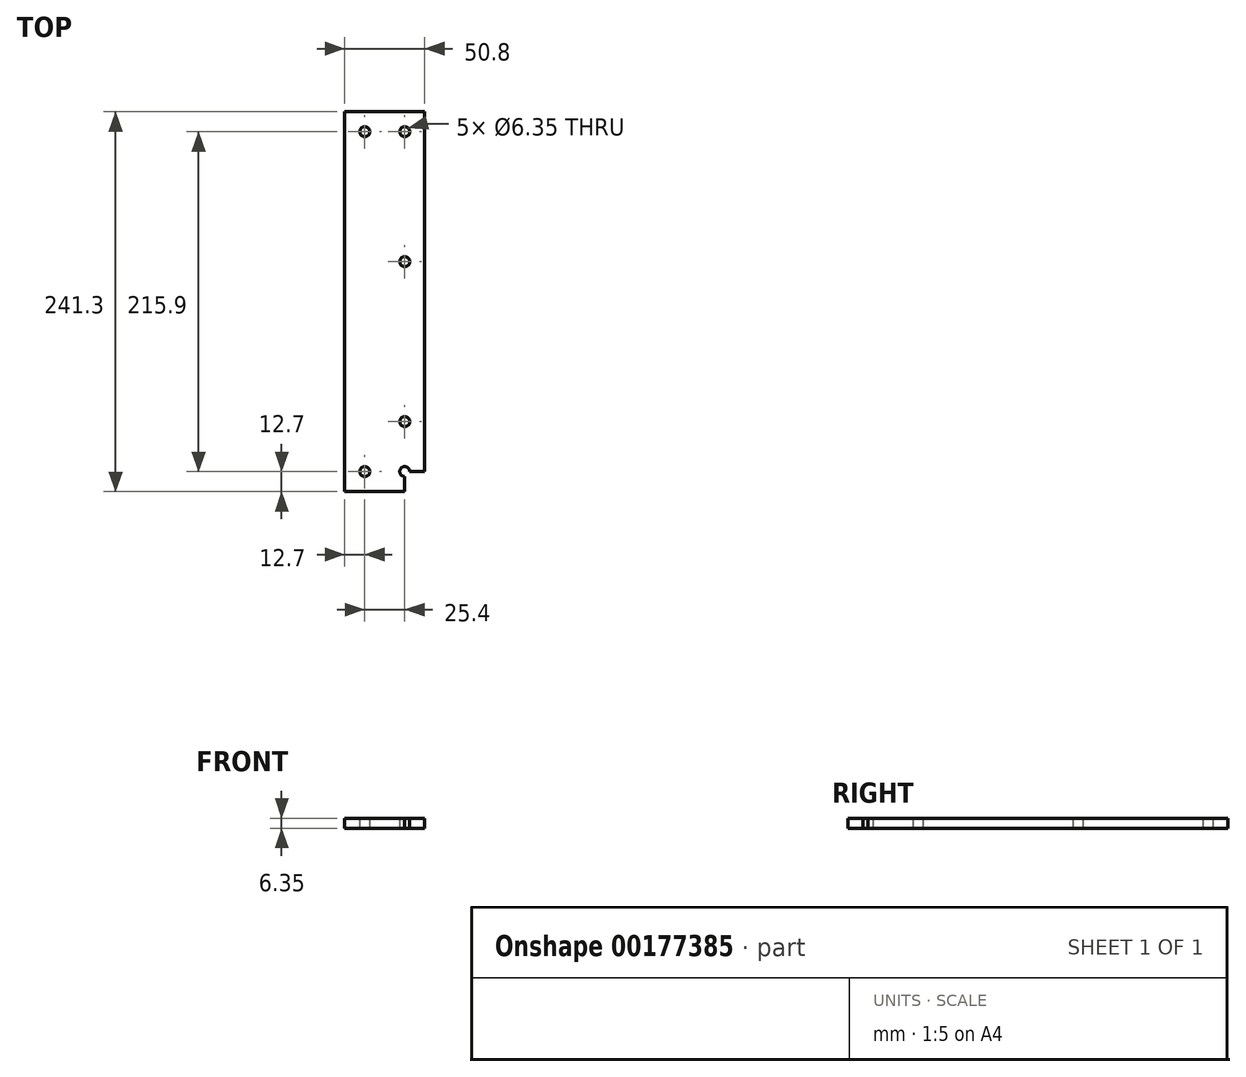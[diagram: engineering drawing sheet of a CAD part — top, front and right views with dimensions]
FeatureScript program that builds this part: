
annotation { "Feature Type Name" : "Feature", "Feature Type Description" : "" }
export const myFeature = defineFeature(function(context is Context, id is Id, definition is map)
    precondition{}
    {
        {
            var Q0;
            Q0=qCreatedBy(makeId("Top.planeOp"),FACE);
            var sketch = newSketch(context, id + "F0", { "sketchPlane" : qUnion([Q0])});
            skLineSegment(sketch, "E0.bottom", {"start": v(25.4, 120.65) * mm, "end": v(-25.4, 120.65) * mm});
            skLineSegment(sketch, "E0.top", {"start": v(25.4, -120.65) * mm, "end": v(-25.4, -120.65) * mm});
            skLineSegment(sketch, "E0.left", {"start": v(25.4, 120.65) * mm, "end": v(25.4, -120.65) * mm});
            skLineSegment(sketch, "E0.right", {"start": v(-25.4, 120.65) * mm, "end": v(-25.4, -120.65) * mm});
            skPoint(sketch, "E0.middle", {"position": v(0, 0) * mm});
            skLineSegment(sketch, "E1", {"start": v(25.4, -120.65) * mm, "end": v(12.7, -120.65) * mm});
            skLineSegment(sketch, "E2", {"start": v(12.7, -120.65) * mm, "end": v(12.7, -107.95) * mm});
            skLineSegment(sketch, "E3", {"start": v(12.7, -107.95) * mm, "end": v(25.4, -107.95) * mm});
            skLineSegment(sketch, "E4", {"start": v(12.7, -107.95) * mm, "end": v(-12.7, -107.95) * mm});
            skLineSegment(sketch, "E5", {"start": v(-12.7, -107.95) * mm, "end": v(-12.7, -120.65) * mm});
            skLineSegment(sketch, "E6", {"start": v(12.7, -107.95) * mm, "end": v(12.7, -76.2) * mm});
            skLineSegment(sketch, "E7", {"start": v(12.7, -76.2) * mm, "end": v(12.7, 25.4) * mm});
            skLineSegment(sketch, "E8", {"start": v(12.7, 25.4) * mm, "end": v(12.7, 57.15) * mm});
            skLineSegment(sketch, "E9", {"start": v(12.7, 120.65) * mm, "end": v(12.7, 107.95) * mm});
            skLineSegment(sketch, "E10", {"start": v(-12.7, -107.95) * mm, "end": v(-12.7, 120.65) * mm});
            skLineSegment(sketch, "E11", {"start": v(-12.7, 120.65) * mm, "end": v(-12.7, 107.95) * mm});
            skCircle(sketch, "E12", {"center": v(-12.7, 107.95) * mm, "radius": 3.18 * mm});
            skCircle(sketch, "E13", {"center": v(12.7, 107.95) * mm, "radius": 3.18 * mm});
            skCircle(sketch, "E14", {"center": v(12.7, -107.95) * mm, "radius": 3.18 * mm});
            skPoint(sketch, "E14.perimeterSnap0", {"position": v(12.7, -114.3) * mm});
            skPoint(sketch, "E14.perimeterSnap1", {"position": v(19.05, -120.65) * mm});
            skCircle(sketch, "E15", {"center": v(-12.7, -107.95) * mm, "radius": 3.18 * mm});
            skCircle(sketch, "E16", {"center": v(12.7, -76.2) * mm, "radius": 3.17 * mm});
            skCircle(sketch, "E17", {"center": v(12.7, 25.4) * mm, "radius": 3.18 * mm});
            skSolve(sketch);
        }
        {
            var Q0;
            {var subQ0=sQuery(id+"F0.wireOp",EDGE,"E0.right");Q0=makeQuery(id+"F0.imprint","IMPRINT",FACE,{"disambiguationData":[TD([[makeQuery(id+"F0.imprint","IMPRINT",EDGE,{"derivedFrom":subQ0}),1.0]])]});}
            var Q1;
            Q1=makeQuery(id+"F0.imprint","IMPRINT",FACE,{"disambiguationData":[TD([[makeQuery(id+"F0.imprint","IMPRINT",EDGE,{"derivedFrom":sQuery(id+"F0.wireOp",EDGE,"E13")}),-1.0]])]});
            var Q2;
            {var subQ0=sQuery(id+"F0.wireOp",EDGE,"E14");var subQ1=sQuery(id+"F0.wireOp",EDGE,"E4");var subQ2=makeQuery(id+"F0.imprint","INTERSECT",VERTEX,{"derivedFrom":[subQ1,subQ0]});Q2=makeQuery(id+"F0.imprint","IMPRINT",FACE,{"disambiguationData":[TD([[makeQuery(id+"F0.imprint","IMPRINT",EDGE,{"disambiguationData":[TD([[subQ2,-1.0]])],"derivedFrom":subQ1}),1.0]])]});}
            var Q3;
            {var subQ6=sQuery(id+"F0.wireOp",EDGE,"E1");Q3=makeQuery(id+"F0.imprint","IMPRINT",FACE,{"disambiguationData":[TD([[makeQuery(id+"F0.imprint","IMPRINT",EDGE,{"derivedFrom":subQ6}),-1.0]])]});}
            extrude(context, id + "F1", {"entities" : qUnion([Q0, Q1, Q2, Q3]), "depth" : 6.35 * mm});
        }
    });
